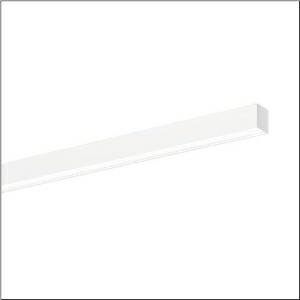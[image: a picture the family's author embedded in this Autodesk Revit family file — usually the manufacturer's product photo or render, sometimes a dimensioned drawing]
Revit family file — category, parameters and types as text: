
# Revit family: silica_21_51mx20tat2w
name_source: partatom
category: Lighting Fixtures
units: mm (PartAtom-declared; Revit-internal decimal feet)

## family parameters
Cut with Voids When Loaded = No
Host = Face
Light Source = No
Part Type = Normal
Room Calculation Point = No
Round Connector Dimension = Use Diameter
Shared = No

## types (1)
- --- (1 x LED, 2400 lm, 20.5 W, 6500K)
    Apparent Load = 21 VA
    CIE Flux Codes = 48 79 96 100 100
    Color Rendering = 80
    Color Temperature = 6500K
    Default Elevation = 1800 mm
    Description = Silica 21, office luminaire, primary optical cover: cover, of PMMA, opal, light emission: direct distribution, primary light characteristic: symmetric, installation type: surface-mounted, LED, rated luminous flux: 2.400lm, luminous efficacy: 112lm/W, light colour: 8tw, colour temperature: 2700..6500K, control gear: DALI DT8, with terminal, 3+2-pole, max. 2.5mm², mains connection: 220..240V, AC, 50/60Hz, rated input power: 21.5W, luminaire housing, of aluminium, traffic white (RAL 9016), length: 1.204mm, width: 53mm, height: 53mm, protection rating (complete): IP20, insulation class (complete): insulation class I (protective earthing), certification: CE, permissible operating ambient temperature: 0..+35°C, standard: EN 50419, packaging unit: 1 piece
    Height = 53 mm
    Lamp = 1 x LED
    Lamp Light Flux = 2400 lm
    Lamp Power = 20.5 W
    Lamp count = 1
    Length = 1204 mm
    Luminous efficacy = 117 lm/W
    Manufacturer = Siteco
    ModVariant = No
    Model = 51MX20TAT2W
    Mounting Place = Ceiling
    Mounting Type = Surface mounted
    Number of Poles = 1
    OnlyDefault = Yes
    Power Factor = 1
    Product Name = Silica 21
    Product group = office luminaire | ceiling mounted
    ProductGroupID = 301
    Protection Class = Protection class I
    Protection Degree = IP 20
    RLX_Detail_Level = 1
    RLX_Emergency_Light_Flux = 0 lm
    RLX_Emergency_Type = 0
    RLX_Emergency_Type_DB = No
    RlxData = <blob elided: 20649 chars, md5=67cbdcac>
    Socket = socket
    Standby Power = 0 W
    System Light Flux = 2400 lm
    System Power = 21 W
    Type Comments = individual setting
    Type Image = l_1335877.jpg
    URL = http://relux.com
    VarID = @adj_139205
    Voltage = 0 V
    Weight = 0.00 kg
    Width = 53 mm

## geometry (parser evidence)
native form markers: Blend x4, Sweep x11
no freeform markers — native parametric forms only
